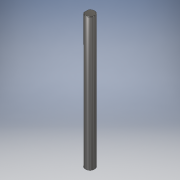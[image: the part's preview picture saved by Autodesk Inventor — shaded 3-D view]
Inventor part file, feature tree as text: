
AUTODESK INVENTOR PART (.ipt)
format: ipt  version: 2018 (Build 220112000, 112)  size: 109,056 bytes
history: native  units: in
note: dims shown in document units (in); Inventor stores cm internally (conversion verified against a paired STEP export)
features: extrude x2, chamfer x2, sketch x2
ambient origin geometry x8: Origin, YZ Plane, XZ Plane, XY Plane, X Axis, Y Axis, Z Axis, Center Point
bodies: Solid1 (feature_tree)
feature tree (6):
  extrude  "Extrusion1"  Depth=2.8346in TaperAngle=0.0deg
  extrude  "Extrusion2"  Depth=0.5906in TaperAngle=0.0deg
  chamfer  "Chamfer1"  Distance=0.0079in Angle=45.0deg
  chamfer  "Chamfer2"  Distance=0.0079in Angle=45.0deg
  sketch  "Sketch1"  dims[d0=0.1969in d1=2.8346in d2=0.0in]
  sketch  "Sketch2"  dims[d3=0.0787in d4=0.5906in d5=0.0in d6=0.0079in d7=0.0787in d8=45.0deg d9=0.0079in d10=0.0787in d11=45.0deg]
